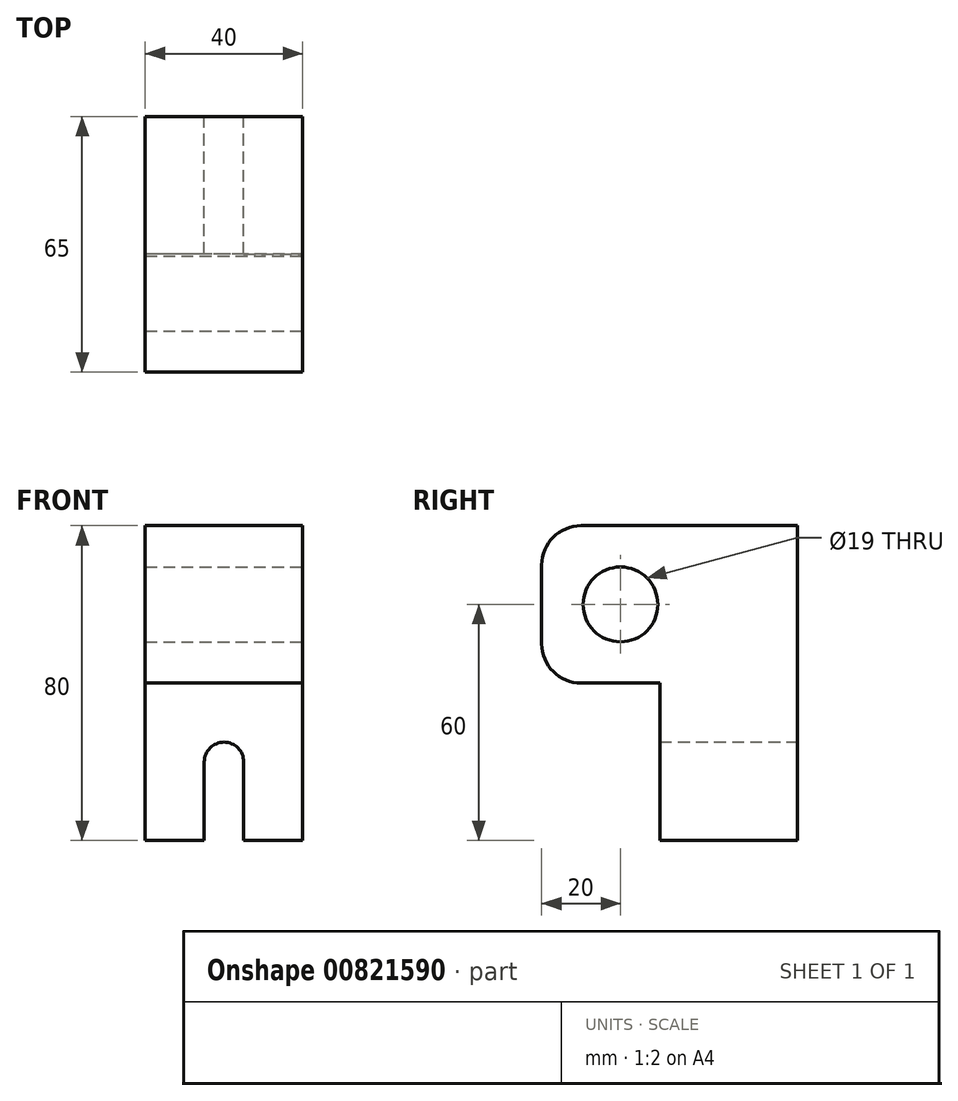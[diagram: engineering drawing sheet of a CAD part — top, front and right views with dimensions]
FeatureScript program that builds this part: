
annotation { "Feature Type Name" : "Feature", "Feature Type Description" : "" }
export const myFeature = defineFeature(function(context is Context, id is Id, definition is map)
    precondition{}
    {
        {
            var Q0;
            Q0=qCreatedBy(makeId("Front.planeOp"),FACE);
            var sketch = newSketch(context, id + "F0", { "sketchPlane" : qUnion([Q0])});
            skLineSegment(sketch, "E0", {"start": v(5, 0) * mm, "end": v(20, 0) * mm});
            skLineSegment(sketch, "E1", {"start": v(-5, 0) * mm, "end": v(-20, 0) * mm});
            skLineSegment(sketch, "E2", {"start": v(20, 0) * mm, "end": v(20, 80) * mm});
            skLineSegment(sketch, "E3", {"start": v(20, 80) * mm, "end": v(-20, 80) * mm});
            skLineSegment(sketch, "E4", {"start": v(-20, 80) * mm, "end": v(-20, 0) * mm});
            skLineSegment(sketch, "E5", {"start": v(-20, 0) * mm, "end": v(-5, 0) * mm});
            skLineSegment(sketch, "E6", {"start": v(-5, 0) * mm, "end": v(-5, 20) * mm});
            skLineSegment(sketch, "E7", {"start": v(5, 0) * mm, "end": v(5, 20) * mm});
            skArc(sketch, "E8", {"start": v(5, 20) * mm, "mid": v(0, 25) * mm, "end": v(-5, 20) * mm});
            skSolve(sketch);
        }
        {
            var Q0;
            Q0 = qSketchRegion(id + "F0", true);
            extrude(context, id + "F1", {"entities" : qUnion([Q0]), "depth" : 35 * mm, "offsetDistance" : 25 * mm});
        }
        {
            var Q0;
            Q0=makeQuery(id+"F1.opExtrude","CAP_FACE",FACE,{"disambiguationData":[OSD([sQuery(id+"F0.wireOp",EDGE,"E0"),sQuery(id+"F0.wireOp",EDGE,"E2"),sQuery(id+"F0.wireOp",EDGE,"E3"),sQuery(id+"F0.wireOp",EDGE,"E4"),sQuery(id+"F0.wireOp",EDGE,"E5"),sQuery(id+"F0.wireOp",EDGE,"E6"),sQuery(id+"F0.wireOp",EDGE,"E7"),sQuery(id+"F0.wireOp",EDGE,"E8")])],"isStart":false});
            var sketch = newSketch(context, id + "F2", { "sketchPlane" : qUnion([Q0])});
            skLineSegment(sketch, "E9", {"start": v(20, 40) * mm, "end": v(-20, 40) * mm});
            skSolve(sketch);
        }
        {
            var Q0;
            Q0 = qSketchRegion(id + "F2", true);
            var Q1;
            {var subQ0=sQuery(id+"F2.wireOp",EDGE,"E9");Q1=makeQuery(id+"F2.imprint","IMPRINT",FACE,{"disambiguationData":[TD([[makeQuery(id+"F2.imprint","IMPRINT",EDGE,{"derivedFrom":subQ0}),-1.0]])]});}
            extrude(context, id + "F3", {"entities" : qUnion([Q0, Q1]), "operationType" : NewBodyOperationType.ADD, "depth" : 20 * mm, "offsetDistance" : 25 * mm});
        }
        {
            var Q0;
            {var subQ0=sQuery(id+"F0.wireOp",EDGE,"E2");Q0=makeQuery(id+"F3.boolean.opBoolean","MERGE",FACE,{"derivedFrom":[makeQuery(id+"F1.opExtrude","SWEPT_FACE",FACE,{"disambiguationData":[OSD([subQ0])]}),makeQuery(id+"F3.opExtrude","SWEPT_FACE",FACE,{"disambiguationData":[OSD([subQ0])]})]});}
            var sketch = newSketch(context, id + "F4", { "sketchPlane" : qUnion([Q0])});
            skCircle(sketch, "E10", {"center": v(-45, 60) * mm, "radius": 9.5 * mm});
            skLineSegment(sketch, "E11", {"start": v(-65, 50) * mm, "end": v(-65, 70) * mm});
            skLineSegment(sketch, "E12", {"start": v(-55, 80) * mm, "end": v(-55, 80) * mm});
            skLineSegment(sketch, "E13", {"start": v(-55, 40) * mm, "end": v(-55, 40) * mm});
            skArc(sketch, "E14.filletArc", {"start": v(-65, 50) * mm, "mid": v(-62.07, 42.93) * mm, "end": v(-55, 40) * mm});
            skArc(sketch, "E15.filletArc", {"start": v(-55, 80) * mm, "mid": v(-62.07, 77.07) * mm, "end": v(-65, 70) * mm});
            skSolve(sketch);
        }
        {
            var Q0;
            Q0=makeQuery(id+"F4.imprint","IMPRINT",FACE,{"disambiguationData":[TD([[makeQuery(id+"F4.imprint","IMPRINT",EDGE,{"derivedFrom":sQuery(id+"F4.wireOp",EDGE,"E11")}),-1.0]])]});
            extrude(context, id + "F5", {"entities" : qUnion([Q0]), "operationType" : NewBodyOperationType.ADD, "depth" : -40 * mm, "offsetDistance" : 25 * mm});
        }
        {
            var Q0;
            Q0=makeQuery(id+"F4.imprint","IMPRINT",FACE,{"disambiguationData":[TD([[makeQuery(id+"F4.imprint","IMPRINT",EDGE,{"derivedFrom":sQuery(id+"F4.wireOp",EDGE,"E10")}),1.0]])]});
            extrude(context, id + "F6", {"entities" : qUnion([Q0]), "operationType" : NewBodyOperationType.REMOVE, "oppositeDirection" : true, "depth" : 40 * mm, "offsetDistance" : 25 * mm});
        }
    });
